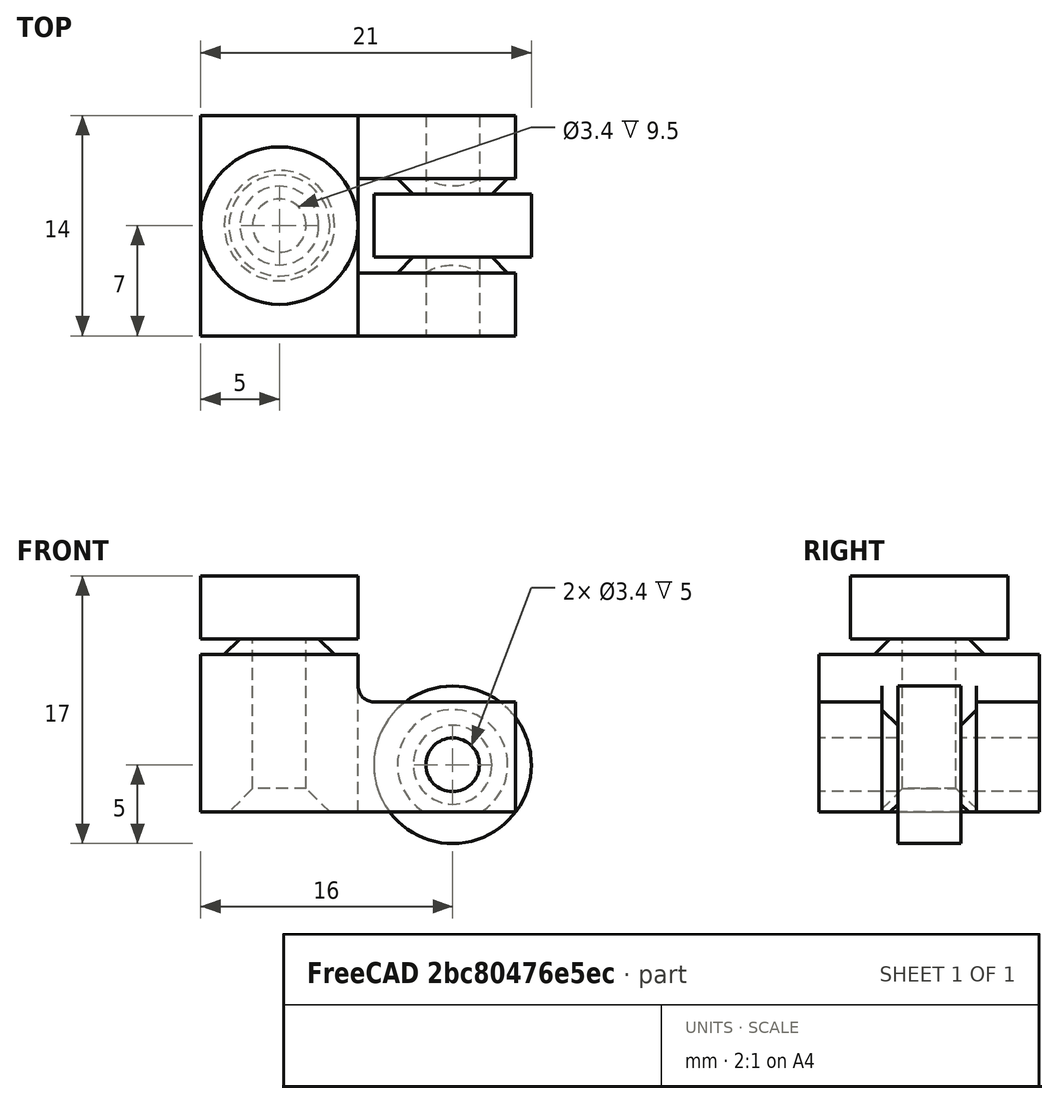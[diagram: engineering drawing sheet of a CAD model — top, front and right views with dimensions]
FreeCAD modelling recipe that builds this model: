
FCSTD DOCUMENT  (FreeCAD 0.18R16146 (Git))
Label: Castor 0.2
License: All rights reserved
LicenseURL: http://en.wikipedia.org/wiki/All_rights_reserved
objects: Part::Cylinder×4, Part::Box×4, Part::Cut×4, Part::Cone×3, Part::MultiFuse×3, Part::Fuse×1, Part::Chamfer×1, Part::Fillet×1
note: 21 computed .brp shape members not serialized (recipe doc carries the construction recipe); baked Part::Feature solids carry a one-line shape summary decoded from their .brp

FEATURE [Part::Cylinder] Cylinder082  label="623 Bearing"
  Angle = 360
  AttacherType = Attacher::AttachEngine3D
  Height = 4
  Placement = pos=(0,0,12) rot=(1,0,0;0rad)
  Radius = 5
FEATURE [Part::Cylinder] Cylinder083  label="623 Bearing001"
  Angle = 360
  AttacherType = Attacher::AttachEngine3D
  Height = 4
  Placement = pos=(11,2,4) rot=(1,0,0;1.5708rad)
  Radius = 5
FEATURE [Part::Cone] Cone
  Angle = 360
  AttacherType = Attacher::AttachEngine3D
  Height = 1
  Placement = pos=(0,0,12) rot=(1,0,0;3.14159rad)
  Radius1 = 2.5
  Radius2 = 3.5
FEATURE [Part::Box] Box  label="Cube"
  AttacherType = Attacher::AttachEngine3D
  Height = 10
  Length = 10
  Placement = pos=(-5,-7,1) rot=(0,0,1;0rad)
  Width = 14
FEATURE [Part::Box] Box001  label="Cube001"
  AttacherType = Attacher::AttachEngine3D
  Height = 7
  Length = 10
  Placement = pos=(5,-7,1) rot=(0,0,1;0rad)
  Width = 14
FEATURE [Part::Cone] Cone001
  Angle = 360
  AttacherType = Attacher::AttachEngine3D
  Height = 1
  Placement = pos=(11,-2,4) rot=(1,0,0;1.5708rad)
  Radius1 = 2.5
  Radius2 = 3.5
FEATURE [Part::Cone] Cone002
  Angle = 360
  AttacherType = Attacher::AttachEngine3D
  Height = 1
  Placement = pos=(11,2,4) rot=(-1,0,0;1.5708rad)
  Radius1 = 2.5
  Radius2 = 3.5
FEATURE [Part::Cylinder] Cylinder084  label="screw"
  Angle = 360
  AttacherType = Attacher::AttachEngine3D
  Height = 18
  Placement = pos=(11,8,4) rot=(1,0,0;1.5708rad)
  Radius = 1.7
FEATURE [Part::Box] Box002  label="Cube002"
  AttacherType = Attacher::AttachEngine3D
  Height = 10
  Length = 11
  Placement = pos=(5,-3,0) rot=(0,0,1;0rad)
  Width = 6
FEATURE [Part::Cut] Cut
  Base = -> Box001
  Tool = -> Box002
FEATURE [Part::Box] Box003  label="Cube003"
  AttacherType = Attacher::AttachEngine3D
  Height = 10
  Length = 10
  Placement = pos=(5,-5,-9) rot=(0,0,1;0rad)
  Width = 10
FEATURE [Part::Fuse] Fusion
  Base = -> Cone001
  Tool = -> Cone002
FEATURE [Part::Cut] Cut001
  Base = -> Fusion
  Tool = -> Box003
FEATURE [Part::MultiFuse] Fusion001
  Shapes = -> [Cut001,Cut]
FEATURE [Part::Cut] Cut002
  Base = -> Fusion001
  Tool = -> Cylinder084
FEATURE [Part::Cylinder] Cylinder
  Angle = 360
  AttacherType = Attacher::AttachEngine3D
  Height = 14
  Radius = 1.7
FEATURE [Part::MultiFuse] Fusion002
  Shapes = -> [Box,Cone]
FEATURE [Part::Cut] Cut003
  Base = -> Fusion002
  Tool = -> Cylinder
FEATURE [Part::MultiFuse] Fusion003
  Shapes = -> [Cut003,Cut002]
FEATURE [Part::Chamfer] Chamfer
  Base = -> Fusion003
  Edges = 1 edges r=1.5: [Edge18]
FEATURE [Part::Fillet] Fillet
  Base = -> Chamfer
  Edges = 2 edges r=1: [Edge25,Edge28]
